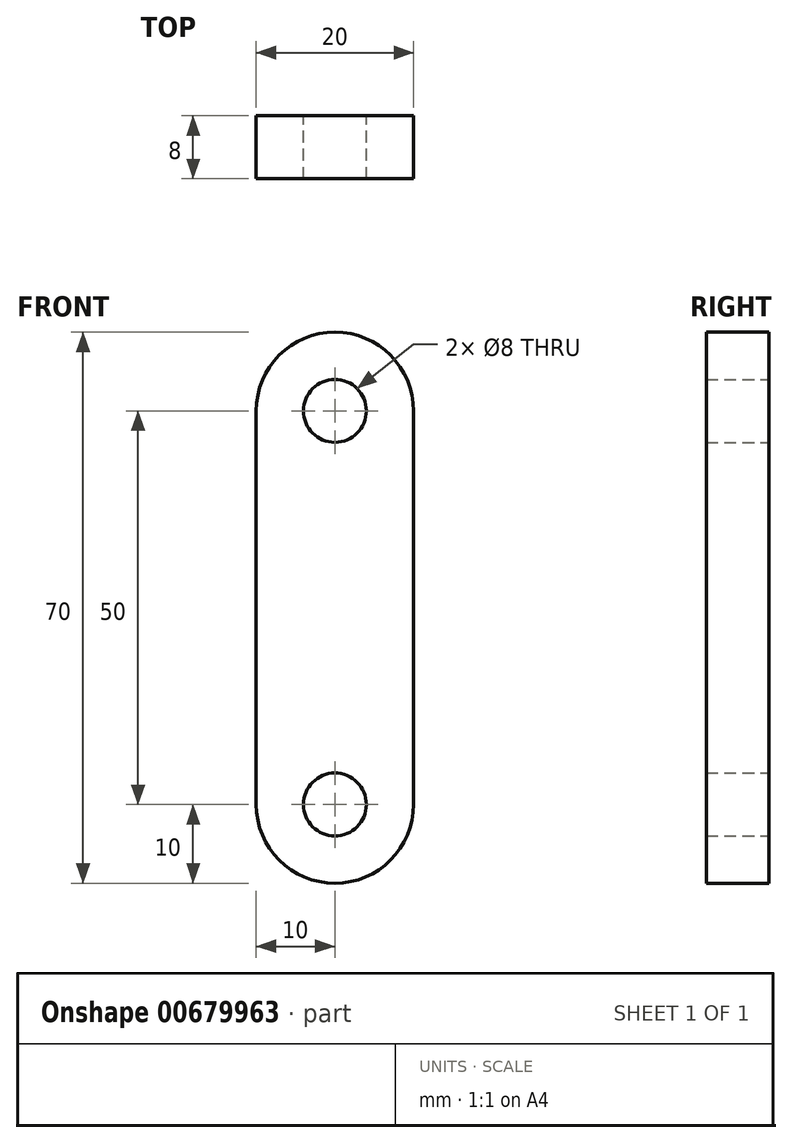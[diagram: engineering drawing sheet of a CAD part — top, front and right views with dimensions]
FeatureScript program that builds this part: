
annotation { "Feature Type Name" : "Feature", "Feature Type Description" : "" }
export const myFeature = defineFeature(function(context is Context, id is Id, definition is map)
    precondition{}
    {
        {
            var Q0;
            Q0=qCreatedBy(makeId("Front.planeOp"),FACE);
            var sketch = newSketch(context, id + "F0", { "sketchPlane" : qUnion([Q0])});
            skArc(sketch, "E0", {"start": v(10, 50) * mm, "mid": v(0, 60) * mm, "end": v(-10, 50) * mm});
            skCircle(sketch, "E1", {"center": v(0, 50) * mm, "radius": 4 * mm});
            skLineSegment(sketch, "E2", {"start": v(-10, 50) * mm, "end": v(-10, 0) * mm});
            skLineSegment(sketch, "E3", {"start": v(10, 50) * mm, "end": v(10, 0) * mm});
            skArc(sketch, "E4", {"start": v(-10, 0) * mm, "mid": v(0, -10) * mm, "end": v(10, 0) * mm});
            skCircle(sketch, "E5", {"center": v(0, 0) * mm, "radius": 4 * mm});
            skSolve(sketch);
        }
        {
            var Q0;
            Q0 = qSketchRegion(id + "F0", true);
            extrude(context, id + "F1", {"entities" : qUnion([Q0]), "depth" : 8 * mm, "offsetDistance" : 25.4 * mm});
        }
    });
